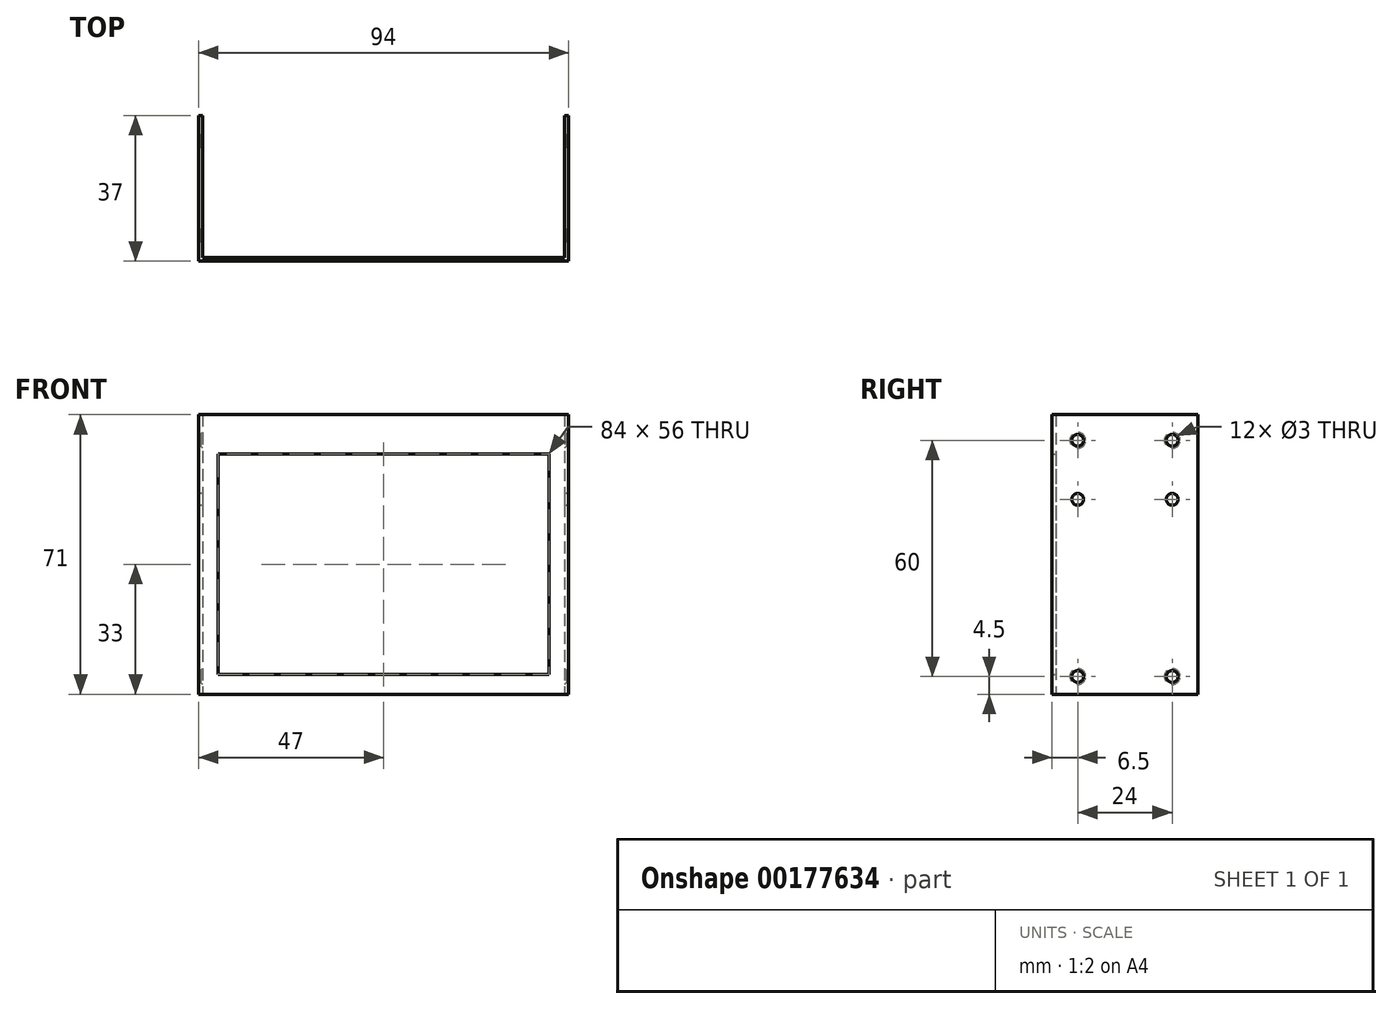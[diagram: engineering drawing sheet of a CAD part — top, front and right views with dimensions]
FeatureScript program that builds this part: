
annotation { "Feature Type Name" : "Feature", "Feature Type Description" : "" }
export const myFeature = defineFeature(function(context is Context, id is Id, definition is map)
    precondition{}
    {
        {
            var Q0;
            Q0=qCreatedBy(makeId("Front.planeOp"),FACE);
            var sketch = newSketch(context, id + "F0", { "sketchPlane" : qUnion([Q0])});
            skLineSegment(sketch, "E0.bottom", {"start": v(47, 35.5) * mm, "end": v(-47, 35.5) * mm});
            skLineSegment(sketch, "E0.top", {"start": v(47, -35.5) * mm, "end": v(-47, -35.5) * mm});
            skLineSegment(sketch, "E0.left", {"start": v(47, 35.5) * mm, "end": v(47, -35.5) * mm});
            skLineSegment(sketch, "E0.right", {"start": v(-47, 35.5) * mm, "end": v(-47, -35.5) * mm});
            skPoint(sketch, "E0.middle", {"position": v(0, 0) * mm});
            skLineSegment(sketch, "E1.bottom", {"start": v(42, 25.5) * mm, "end": v(-42, 25.5) * mm});
            skLineSegment(sketch, "E1.top", {"start": v(42, -30.5) * mm, "end": v(-42, -30.5) * mm});
            skLineSegment(sketch, "E1.left", {"start": v(42, 25.5) * mm, "end": v(42, -30.5) * mm});
            skLineSegment(sketch, "E1.right", {"start": v(-42, 25.5) * mm, "end": v(-42, -30.5) * mm});
            skPoint(sketch, "E1.middle", {"position": v(0, -2.5) * mm});
            skSolve(sketch);
        }
        {
            var Q0;
            Q0=qSketchRegion(id+"F0",true);
            extrude(context, id + "F1", {"entities" : qUnion([Q0]), "depth" : 1 * mm});
        }
        {
            var Q0;
            Q0=makeQuery(id+"F1.opExtrude","CAP_FACE",FACE,{"disambiguationData":[OSD([sQuery(id+"F0.wireOp",EDGE,"E0.bottom"),sQuery(id+"F0.wireOp",EDGE,"E0.top"),sQuery(id+"F0.wireOp",EDGE,"E0.left"),sQuery(id+"F0.wireOp",EDGE,"E0.right"),sQuery(id+"F0.wireOp",EDGE,"SgeA5SFv-ycm6-KkIP-0Kqd-vPRJc91bn5sW.bottom"),sQuery(id+"F0.wireOp",EDGE,"SgeA5SFv-ycm6-KkIP-0Kqd-vPRJc91bn5sW.top"),sQuery(id+"F0.wireOp",EDGE,"SgeA5SFv-ycm6-KkIP-0Kqd-vPRJc91bn5sW.left"),sQuery(id+"F0.wireOp",EDGE,"SgeA5SFv-ycm6-KkIP-0Kqd-vPRJc91bn5sW.right")])],"isStart":true});
            var sketch = newSketch(context, id + "F2", { "sketchPlane" : qUnion([Q0])});
            skLineSegment(sketch, "E2.bottom", {"start": v(-47, 35.5) * mm, "end": v(-46, 35.5) * mm});
            skLineSegment(sketch, "E2.top", {"start": v(-47, -35.5) * mm, "end": v(-46, -35.5) * mm});
            skLineSegment(sketch, "E2.left", {"start": v(-47, 35.5) * mm, "end": v(-47, -35.5) * mm});
            skLineSegment(sketch, "E2.right", {"start": v(-46, 35.5) * mm, "end": v(-46, -35.5) * mm});
            skLineSegment(sketch, "E3.bottom", {"start": v(47, 35.5) * mm, "end": v(46, 35.5) * mm});
            skLineSegment(sketch, "E3.top", {"start": v(47, -35.5) * mm, "end": v(46, -35.5) * mm});
            skLineSegment(sketch, "E3.left", {"start": v(47, 35.5) * mm, "end": v(47, -35.5) * mm});
            skLineSegment(sketch, "E3.right", {"start": v(46, 35.5) * mm, "end": v(46, -35.5) * mm});
            skSolve(sketch);
        }
        {
            var Q0;
            Q0 = qSketchRegion(id + "F2", true);
            extrude(context, id + "F3", {"entities" : qUnion([Q0]), "operationType" : NewBodyOperationType.ADD, "depth" : 36 * mm});
        }
        {
            var Q0;
            Q0=makeQuery(id+"F3.boolean.opBoolean","MERGE",FACE,{"derivedFrom":[makeQuery(id+"F1.opExtrude","SWEPT_FACE",FACE,{"disambiguationData":[OSD([sQuery(id+"F0.wireOp",EDGE,"E0.right")])]}),makeQuery(id+"F3.opExtrude","SWEPT_FACE",FACE,{"disambiguationData":[OSD([sQuery(id+"F2.wireOp",EDGE,"E3.left")])]})]});
            var sketch = newSketch(context, id + "F4", { "sketchPlane" : qUnion([Q0])});
            skCircle(sketch, "E4", {"center": v(-29.5, -31) * mm, "radius": 1.5 * mm});
            skCircle(sketch, "E5", {"center": v(-5.5, -31) * mm, "radius": 1.5 * mm});
            skCircle(sketch, "E6", {"center": v(-29.5, 29) * mm, "radius": 1.5 * mm});
            skCircle(sketch, "E7", {"center": v(-5.5, 29) * mm, "radius": 1.5 * mm});
            skLineSegment(sketch, "E8", {"start": v(-29.5, 29) * mm, "end": v(-29.5, -31) * mm, "construction": true});
            skLineSegment(sketch, "E9", {"start": v(-5.5, 29) * mm, "end": v(-5.5, -31) * mm, "construction": true});
            skCircle(sketch, "E10", {"center": v(-29.5, 14) * mm, "radius": 1.5 * mm});
            skCircle(sketch, "E11", {"center": v(-5.5, 14) * mm, "radius": 1.5 * mm});
            skSolve(sketch);
        }
        {
            var Q0;
            Q0 = qSketchRegion(id + "F4", true);
            extrude(context, id + "F5", {"entities" : qUnion([Q0]), "operationType" : NewBodyOperationType.REMOVE, "oppositeDirection" : true, "depth" : 100 * mm});
        }
        {
            var Q0;
            Q0=makeQuery(id+"F5.boolean.opBoolean","INTERSECT",EDGE,{"derivedFrom":[makeQuery(id+"F3.opExtrude","SWEPT_FACE",FACE,{"disambiguationData":[OSD([sQuery(id+"F2.wireOp",EDGE,"E3.right")])]}),makeQuery(id+"F5.opExtrude","SWEPT_FACE",FACE,{"disambiguationData":[OSD([sQuery(id+"F4.wireOp",EDGE,"E4")])]})]});
            var Q1;
            Q1=makeQuery(id+"F5.boolean.opBoolean","INTERSECT",EDGE,{"derivedFrom":[makeQuery(id+"F3.opExtrude","SWEPT_FACE",FACE,{"disambiguationData":[OSD([sQuery(id+"F2.wireOp",EDGE,"E3.right")])]}),makeQuery(id+"F5.opExtrude","SWEPT_FACE",FACE,{"disambiguationData":[OSD([sQuery(id+"F4.wireOp",EDGE,"E5")])]})]});
            var Q2;
            Q2=makeQuery(id+"F5.boolean.opBoolean","INTERSECT",EDGE,{"derivedFrom":[makeQuery(id+"F3.opExtrude","SWEPT_FACE",FACE,{"disambiguationData":[OSD([sQuery(id+"F2.wireOp",EDGE,"E2.right")])]}),makeQuery(id+"F5.opExtrude","SWEPT_FACE",FACE,{"disambiguationData":[OSD([sQuery(id+"F4.wireOp",EDGE,"E5")])]})]});
            var Q3;
            Q3=makeQuery(id+"F5.boolean.opBoolean","INTERSECT",EDGE,{"derivedFrom":[makeQuery(id+"F3.opExtrude","SWEPT_FACE",FACE,{"disambiguationData":[OSD([sQuery(id+"F2.wireOp",EDGE,"E2.right")])]}),makeQuery(id+"F5.opExtrude","SWEPT_FACE",FACE,{"disambiguationData":[OSD([sQuery(id+"F4.wireOp",EDGE,"E4")])]})]});
            chamfer(context, id + "F6", {"entities" : qUnion([Q0, Q1, Q2, Q3]), "width" : .5 * mm, "tangentPropagation" : true});
        }
        {
            var Q0;
            Q0=makeQuery(id+"F5.boolean.opBoolean","INTERSECT",EDGE,{"derivedFrom":[makeQuery(id+"F3.opExtrude","SWEPT_FACE",FACE,{"disambiguationData":[OSD([sQuery(id+"F2.wireOp",EDGE,"E2.right")])]}),makeQuery(id+"F5.opExtrude","SWEPT_FACE",FACE,{"disambiguationData":[OSD([sQuery(id+"F4.wireOp",EDGE,"E6")])]})]});
            var Q1;
            Q1=makeQuery(id+"F5.boolean.opBoolean","INTERSECT",EDGE,{"derivedFrom":[makeQuery(id+"F3.opExtrude","SWEPT_FACE",FACE,{"disambiguationData":[OSD([sQuery(id+"F2.wireOp",EDGE,"E2.right")])]}),makeQuery(id+"F5.opExtrude","SWEPT_FACE",FACE,{"disambiguationData":[OSD([sQuery(id+"F4.wireOp",EDGE,"E7")])]})]});
            var Q2;
            Q2=makeQuery(id+"F5.boolean.opBoolean","INTERSECT",EDGE,{"derivedFrom":[makeQuery(id+"F3.opExtrude","SWEPT_FACE",FACE,{"disambiguationData":[OSD([sQuery(id+"F2.wireOp",EDGE,"E3.right")])]}),makeQuery(id+"F5.opExtrude","SWEPT_FACE",FACE,{"disambiguationData":[OSD([sQuery(id+"F4.wireOp",EDGE,"E7")])]})]});
            var Q3;
            Q3=makeQuery(id+"F5.boolean.opBoolean","INTERSECT",EDGE,{"derivedFrom":[makeQuery(id+"F3.opExtrude","SWEPT_FACE",FACE,{"disambiguationData":[OSD([sQuery(id+"F2.wireOp",EDGE,"E3.right")])]}),makeQuery(id+"F5.opExtrude","SWEPT_FACE",FACE,{"disambiguationData":[OSD([sQuery(id+"F4.wireOp",EDGE,"E6")])]})]});
            chamfer(context, id + "F7", {"entities" : qUnion([Q0, Q1, Q2, Q3]), "width" : .5 * mm, "tangentPropagation" : true});
        }
    });
